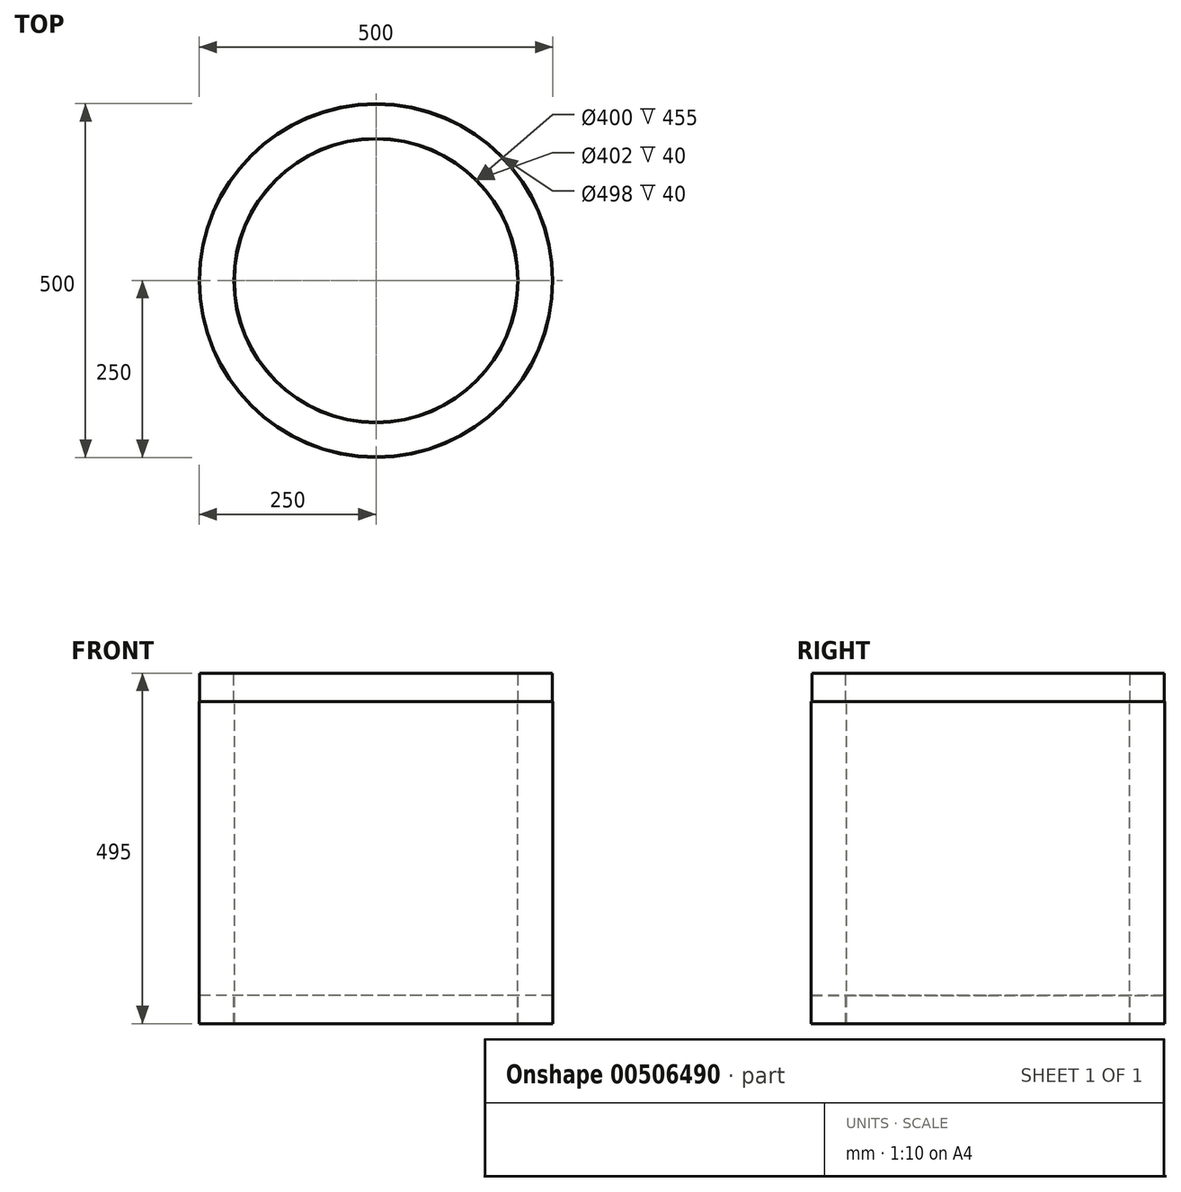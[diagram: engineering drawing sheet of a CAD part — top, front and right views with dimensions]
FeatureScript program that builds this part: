
annotation { "Feature Type Name" : "Feature", "Feature Type Description" : "" }
export const myFeature = defineFeature(function(context is Context, id is Id, definition is map)
    precondition{}
    {
        {
            var Q0;
            Q0=qCreatedBy(makeId("Front.planeOp"),FACE);
            var sketch = newSketch(context, id + "F0", { "sketchPlane" : qUnion([Q0])});
            skLineSegment(sketch, "E0", {"start": v(0, 74.87) * mm, "end": v(0, -73.71) * mm, "construction": true});
            skLineSegment(sketch, "E1", {"start": v(0, 374.84) * mm, "end": v(0, -528.94) * mm, "construction": true});
            skLineSegment(sketch, "E2", {"start": v(-200, -489.75) * mm, "end": v(-200, -34.75) * mm});
            skLineSegment(sketch, "E3", {"start": v(-200, -34.75) * mm, "end": v(-201, -34.75) * mm});
            skLineSegment(sketch, "E4", {"start": v(-201, -34.75) * mm, "end": v(-201, 5.25) * mm});
            skLineSegment(sketch, "E5", {"start": v(-201, 5.25) * mm, "end": v(-249, 5.25) * mm});
            skLineSegment(sketch, "E6", {"start": v(-249, 5.25) * mm, "end": v(-249, -34.75) * mm});
            skLineSegment(sketch, "E7", {"start": v(-249, -34.75) * mm, "end": v(-250, -34.75) * mm});
            skLineSegment(sketch, "E8", {"start": v(-250, -34.75) * mm, "end": v(-250, -489.75) * mm});
            skLineSegment(sketch, "E9", {"start": v(-250, -489.75) * mm, "end": v(-249, -489.75) * mm});
            skLineSegment(sketch, "E10", {"start": v(-249, -489.75) * mm, "end": v(-249, -449.75) * mm});
            skLineSegment(sketch, "E11", {"start": v(-249, -449.75) * mm, "end": v(-201, -449.75) * mm});
            skLineSegment(sketch, "E12", {"start": v(-201, -449.75) * mm, "end": v(-201, -489.75) * mm});
            skLineSegment(sketch, "E13", {"start": v(-201, -489.75) * mm, "end": v(-200, -489.75) * mm});
            skSolve(sketch);
        }
        {
            var Q0;
            Q0=qSketchRegion(id+"F0",true);
            var Q1;
            Q1=sQuery(id+"F0.wireOp",EDGE,"E1");
            revolve(context, id + "F1", {"entities" : qUnion([Q0]), "axis" : qUnion([Q1]), "revolveType" : RevolveType.FULL});
        }
    });
